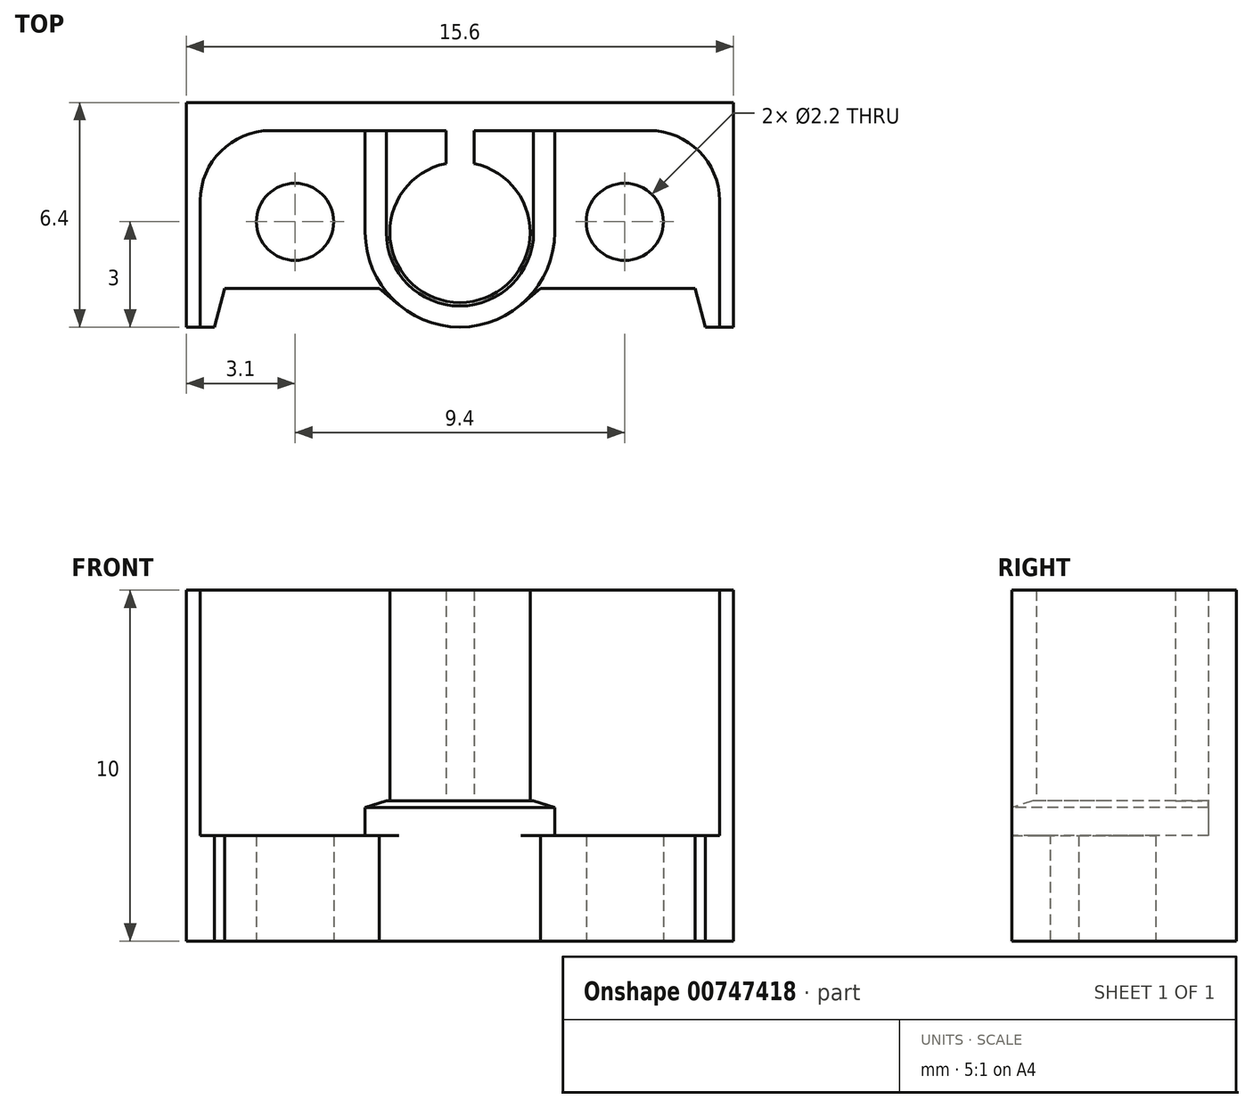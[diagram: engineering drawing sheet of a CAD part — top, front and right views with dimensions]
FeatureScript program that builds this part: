
annotation { "Feature Type Name" : "Feature", "Feature Type Description" : "" }
export const myFeature = defineFeature(function(context is Context, id is Id, definition is map)
    precondition{}
    {
        {
            var Q0;
            Q0=qCreatedBy(makeId("Top.planeOp"),FACE);
            var sketch = newSketch(context, id + "F0", { "sketchPlane" : qUnion([Q0])});
            skArc(sketch, "E0", {"start": v(-0.4, 1.96) * mm, "mid": v(0, -2) * mm, "end": v(0.4, 1.96) * mm});
            skLineSegment(sketch, "E1", {"start": v(-7.4, -2.7) * mm, "end": v(-7.4, 0.9) * mm});
            skLineSegment(sketch, "E2", {"start": v(-5.4, 2.9) * mm, "end": v(-0.4, 2.9) * mm});
            skLineSegment(sketch, "E3", {"start": v(7.4, 0.9) * mm, "end": v(7.4, -2.7) * mm});
            skLineSegment(sketch, "E4", {"start": v(7.4, -2.7) * mm, "end": v(7.8, -2.7) * mm});
            skLineSegment(sketch, "E5", {"start": v(7.8, -2.7) * mm, "end": v(7.8, 3.7) * mm});
            skLineSegment(sketch, "E6", {"start": v(7.8, 3.7) * mm, "end": v(-7.8, 3.7) * mm});
            skLineSegment(sketch, "E7", {"start": v(-7.8, 3.7) * mm, "end": v(-7.8, -2.7) * mm});
            skLineSegment(sketch, "E8", {"start": v(-7.8, -2.7) * mm, "end": v(-7.4, -2.7) * mm});
            skLineSegment(sketch, "E9", {"start": v(-0.4, 1.96) * mm, "end": v(-0.4, 2.9) * mm});
            skLineSegment(sketch, "E10", {"start": v(0.4, 1.96) * mm, "end": v(0.4, 2.9) * mm});
            skLineSegment(sketch, "E11.trimOffspring", {"start": v(0.4, 2.9) * mm, "end": v(5.4, 2.9) * mm});
            skPoint(sketch, "E12.visualSharp", {"position": v(-7.4, 2.9) * mm});
            skArc(sketch, "E12.filletArc", {"start": v(-5.4, 2.9) * mm, "mid": v(-6.81, 2.31) * mm, "end": v(-7.4, 0.9) * mm});
            skPoint(sketch, "E13.visualSharp", {"position": v(7.4, 2.9) * mm});
            skArc(sketch, "E13.filletArc", {"start": v(7.4, 0.9) * mm, "mid": v(6.81, 2.31) * mm, "end": v(5.4, 2.9) * mm});
            skLineSegment(sketch, "E14", {"start": v(-2.1, 1.96) * mm, "end": v(-7.13, -1.56) * mm, "construction": true});
            skLineSegment(sketch, "E15", {"start": v(-7.13, -1.56) * mm, "end": v(-7.13, -5.12) * mm, "construction": true});
            skLineSegment(sketch, "E16", {"start": v(-7.13, -5.12) * mm, "end": v(7.13, -5.12) * mm, "construction": true});
            skLineSegment(sketch, "E17", {"start": v(7.13, -5.12) * mm, "end": v(7.13, -1.56) * mm, "construction": true});
            skLineSegment(sketch, "E18", {"start": v(7.13, -1.56) * mm, "end": v(2.1, 1.96) * mm, "construction": true});
            skLineSegment(sketch, "E19", {"start": v(2.1, 1.96) * mm, "end": v(1.65, 1.3) * mm, "construction": true});
            skArc(sketch, "E20", {"start": v(-1.65, 1.3) * mm, "mid": v(0, -2.1) * mm, "end": v(1.65, 1.3) * mm, "construction": true});
            skLineSegment(sketch, "E21", {"start": v(-2.1, 1.96) * mm, "end": v(-1.65, 1.3) * mm, "construction": true});
            skSolve(sketch);
        }
        {
            var Q0;
            Q0=qSketchRegion(id+"F0",true);
            extrude(context, id + "F1", {"entities" : qUnion([Q0]), "depth" : 7 * mm, "offsetDistance" : 25 * mm});
        }
        {
            var Q0;
            Q0=makeQuery(id+"F1.opExtrude","CAP_FACE",FACE,{"disambiguationData":[OSD([sQuery(id+"F0.wireOp",EDGE,"E0"),sQuery(id+"F0.wireOp",EDGE,"E1"),sQuery(id+"F0.wireOp",EDGE,"E2"),sQuery(id+"F0.wireOp",EDGE,"E3"),sQuery(id+"F0.wireOp",EDGE,"E4"),sQuery(id+"F0.wireOp",EDGE,"E5"),sQuery(id+"F0.wireOp",EDGE,"E6"),sQuery(id+"F0.wireOp",EDGE,"E7"),sQuery(id+"F0.wireOp",EDGE,"E8"),sQuery(id+"F0.wireOp",EDGE,"E9"),sQuery(id+"F0.wireOp",EDGE,"E10"),sQuery(id+"F0.wireOp",EDGE,"E11.trimOffspring"),sQuery(id+"F0.wireOp",EDGE,"E12.filletArc"),sQuery(id+"F0.wireOp",EDGE,"E13.filletArc")])],"isStart":true});
            var sketch = newSketch(context, id + "F2", { "sketchPlane" : qUnion([Q0])});
            skLineSegment(sketch, "E22.bottom", {"start": v(-7.8, -3.7) * mm, "end": v(7.8, -3.7) * mm});
            skLineSegment(sketch, "E22.top", {"start": v(-7.8, 2.7) * mm, "end": v(7.8, 2.7) * mm});
            skLineSegment(sketch, "E22.left", {"start": v(-7.8, -3.7) * mm, "end": v(-7.8, 2.7) * mm});
            skLineSegment(sketch, "E22.right", {"start": v(7.8, -3.7) * mm, "end": v(7.8, 2.7) * mm});
            skSolve(sketch);
        }
        {
            var Q0;
            Q0=qSketchRegion(id+"F2",true);
            extrude(context, id + "F3", {"entities" : qUnion([Q0]), "operationType" : NewBodyOperationType.ADD, "depth" : 3 * mm, "offsetDistance" : 25 * mm});
        }
        {
            var Q0;
            Q0=makeQuery(id+"F3.opExtrude","CAP_FACE",FACE,{"disambiguationData":[OSD([sQuery(id+"F2.wireOp",EDGE,"E22.bottom"),sQuery(id+"F2.wireOp",EDGE,"E22.top"),sQuery(id+"F2.wireOp",EDGE,"E22.left"),sQuery(id+"F2.wireOp",EDGE,"E22.right")])],"isStart":true});
            var sketch = newSketch(context, id + "F4", { "sketchPlane" : qUnion([Q0])});
            skArc(sketch, "E23", {"start": v(-2.7, 0) * mm, "mid": v(0, -2.7) * mm, "end": v(2.7, 0) * mm});
            skLineSegment(sketch, "E24", {"start": v(2.7, 0) * mm, "end": v(2.7, 2.9) * mm});
            skLineSegment(sketch, "E25", {"start": v(2.7, 2.9) * mm, "end": v(-2.7, 2.9) * mm});
            skLineSegment(sketch, "E26", {"start": v(-2.7, 2.9) * mm, "end": v(-2.7, 0) * mm});
            skSolve(sketch);
        }
        {
            var Q0;
            Q0=qSketchRegion(id+"F4",true);
            extrude(context, id + "F5", {"entities" : qUnion([Q0]), "operationType" : NewBodyOperationType.ADD, "depth" : 1 * mm, "offsetDistance" : 25 * mm});
        }
        {
            var Q0;
            Q0=makeQuery(id+"F5.opExtrude","CAP_EDGE",EDGE,{"disambiguationData":[OSD([sQuery(id+"F4.wireOp",EDGE,"E23")])],"isStart":false});
            chamfer(context, id + "F6", {"entities" : qUnion([Q0]), "chamferType" : ChamferType.TWO_OFFSETS, "width1" : 0.6 * mm, "oppositeDirection" : false, "width2" : 0.2 * mm, "tangentPropagation" : true});
        }
        {
            var Q0;
            {var subQ0=sQuery(id+"F2.wireOp",EDGE,"E22.top");var subQ1=makeQuery(id+"F3.opExtrude","CAP_FACE",FACE,{"disambiguationData":[OSD([sQuery(id+"F2.wireOp",EDGE,"E22.bottom"),subQ0,sQuery(id+"F2.wireOp",EDGE,"E22.left"),sQuery(id+"F2.wireOp",EDGE,"E22.right")])],"isStart":true});Q0=makeQuery(id+"F5.boolean.opBoolean","SPLIT",FACE,{"disambiguationData":[TD([makeQuery(id+"F1.opExtrude","SWEPT_FACE",FACE,{"disambiguationData":[OSD([sQuery(id+"F0.wireOp",EDGE,"E1")])]})])],"derivedFrom":subQ1});}
            var sketch = newSketch(context, id + "F7", { "sketchPlane" : qUnion([Q0])});
            skLineSegment(sketch, "E27", {"start": v(-1.74, -2.07) * mm, "end": v(-2.3, -1.6) * mm});
            skLineSegment(sketch, "E28", {"start": v(-6.7, -1.6) * mm, "end": v(-7, -2.7) * mm});
            skLineSegment(sketch, "E29", {"start": v(-7, -2.7) * mm, "end": v(0, -2.7) * mm});
            skArc(sketch, "E30.0", {"start": v(-1.74, -2.07) * mm, "mid": v(-0.92, -2.54) * mm, "end": v(0, -2.7) * mm});
            skPoint(sketch, "E31.orphan", {"position": v(-2.7, 0) * mm});
            skLineSegment(sketch, "E32", {"start": v(0, -2.7) * mm, "end": v(0, 0) * mm, "construction": true});
            skPoint(sketch, "E33.MirrorP", {"position": v(2.7, 0) * mm});
            skLineSegment(sketch, "E34.MirrorCS", {"start": v(7, -2.7) * mm, "end": v(0, -2.7) * mm});
            skArc(sketch, "E35.MirrorCS", {"start": v(1.74, -2.07) * mm, "mid": v(0.92, -2.54) * mm, "end": v(0, -2.7) * mm});
            skLineSegment(sketch, "E36", {"start": v(-6.7, -1.6) * mm, "end": v(-2.3, -1.6) * mm});
            skPoint(sketch, "E37.orphan", {"position": v(-5.9, 1.42) * mm});
            skLineSegment(sketch, "E38.MirrorCS", {"start": v(1.74, -2.07) * mm, "end": v(2.3, -1.6) * mm});
            skLineSegment(sketch, "E39.MirrorCS", {"start": v(6.7, -1.6) * mm, "end": v(7, -2.7) * mm});
            skLineSegment(sketch, "E40.MirrorCS", {"start": v(6.7, -1.6) * mm, "end": v(2.3, -1.6) * mm});
            skSolve(sketch);
        }
        {
            var Q0;
            Q0 = qSketchRegion(id + "F7", true);
            extrude(context, id + "F8", {"entities" : qUnion([Q0]), "operationType" : NewBodyOperationType.REMOVE, "endBound" : BoundingType.UP_TO_NEXT, "oppositeDirection" : true, "depth" : 25 * mm, "offsetDistance" : 25 * mm});
        }
        {
            var Q0;
            Q0=makeQuery(id+"F3.opExtrude","CAP_FACE",FACE,{"disambiguationData":[OSD([sQuery(id+"F2.wireOp",EDGE,"E22.bottom"),sQuery(id+"F2.wireOp",EDGE,"E22.top"),sQuery(id+"F2.wireOp",EDGE,"E22.left"),sQuery(id+"F2.wireOp",EDGE,"E22.right")])],"isStart":false});
            var sketch = newSketch(context, id + "F9", { "sketchPlane" : qUnion([Q0])});
            skCircle(sketch, "E41", {"center": v(-4.7, -0.3) * mm, "radius": 1.1 * mm});
            skCircle(sketch, "E42", {"center": v(4.7, -0.3) * mm, "radius": 1.1 * mm});
            skLineSegment(sketch, "E43", {"start": v(-4.7, -0.3) * mm, "end": v(4.7, -0.3) * mm, "construction": true});
            skLineSegment(sketch, "E44", {"start": v(0, -0.3) * mm, "end": v(0, -3.7) * mm, "construction": true});
            skSolve(sketch);
        }
        {
            var Q0;
            Q0 = qSketchRegion(id + "F9", true);
            extrude(context, id + "F10", {"entities" : qUnion([Q0]), "operationType" : NewBodyOperationType.REMOVE, "endBound" : BoundingType.UP_TO_NEXT, "oppositeDirection" : true, "depth" : 25 * mm, "offsetDistance" : 25 * mm});
        }
    });
